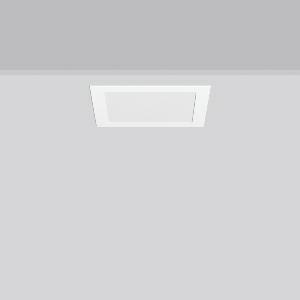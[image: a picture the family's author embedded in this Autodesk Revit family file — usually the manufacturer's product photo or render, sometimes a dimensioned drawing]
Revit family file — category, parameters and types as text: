
# Revit family: toledo_flat_square_e_901487_002_1_1115
name_source: partatom
category: Lighting Fixtures
units: mm (PartAtom-declared; Revit-internal decimal feet)

## family parameters
Cut with Voids When Loaded = No
Host = Face
Light Source = No
Part Type = Normal
Room Calculation Point = No
Round Connector Dimension = Use Diameter
Shared = No

## types (1)
- TOLEDO FLAT square E (1 x LED Modul 840, 1800 lm, 4000)
    Apparent Load = 17 VA
    CIE Flux Codes = 49 80 96 100 100
    Color Rendering = 80
    Color Temperature = 4000
    Default Elevation = 1800 mm
    Description = Series: TOLEDO FLAT square
Ultra thin recessed downlight. Housing: die-cast aluminium. Light guide and diffuser made of non-yellowing PMMA, opal matt. Ceiling installation with spring system. Mounting depth depends on ceiling strength. Suitable for through-wiring with separately available accessories. Surface mounted housing as accessory for all sizes. Retrofittable decorative cylinders made of chintz fabric as accessory, optional with satin finish plastic diffuser. Through-wiring box (5 pole) available as accessory. 
Colour: white
Length: 225 mm
Width: 225 mm
Height: 3 mm
Cut-out length: 208 mm
Cut-out width: 208 mm
Recess height: 29-56 mm
Luminaire: recess height: 31-51 mm
Lamp: LED
Socket: without socket
Colour temperature: 4000K
Colour rendering index (CRI): 80
System power: 17 W
Rated luminous flux: 1800 lm
Luminous efficiency: 106 lm/W
Control gear: Regulated power supply
Protection class: II
Type of protection: IP 54
    Height = 0 mm  [stored 0 ft]
    Lamp = 1 x LED Modul 840
    Lamp Light Flux = 1800 lm
    Lamp count = 1
    Length = 225 mm
    Lifetime = 50000 h
    Luminous efficacy = 106 lm/W
    Manufacturer = RZB
    ModVariant = No
    Model = 901487.002.1
    Mounting Place = Ceiling
    Mounting Type = Recessed
    Number of Poles = 1
    OnlyDefault = Yes
    Power Factor = 1
    Product Name = TOLEDO FLAT square E
    Product group = Recessed downlights
    ProductGroupID = 402
    Protection Class = Protection class II
    Protection Degree = IP 20
    RLX_Detail_Level = 1
    RLX_Emergency_Light_Flux = 0 lm
    RLX_Emergency_Type = 0
    RLX_Emergency_Type_DB = No
    RlxData = <blob elided: 58937 chars, md5=67e24fde>
    Socket = socket
    Standby Power = 0 W
    System Light Flux = 1800 lm
    System Power = 17 W
    Type Comments = Product without accessories
    Type Image = 901487.002.jpg
    URL = http://relux.com
    VarID = ---
    Voltage = 230 V
    Voltage Range = 220-240 V
    Weight = 0.00 kg
    Width = 225 mm

note: [stored X ft] marks values corroborated as IEEE doubles in the binary element streams (Revit-internal decimal feet)

## geometry (parser evidence)
native form markers: Blend x4, Sweep x10
no freeform markers — native parametric forms only
